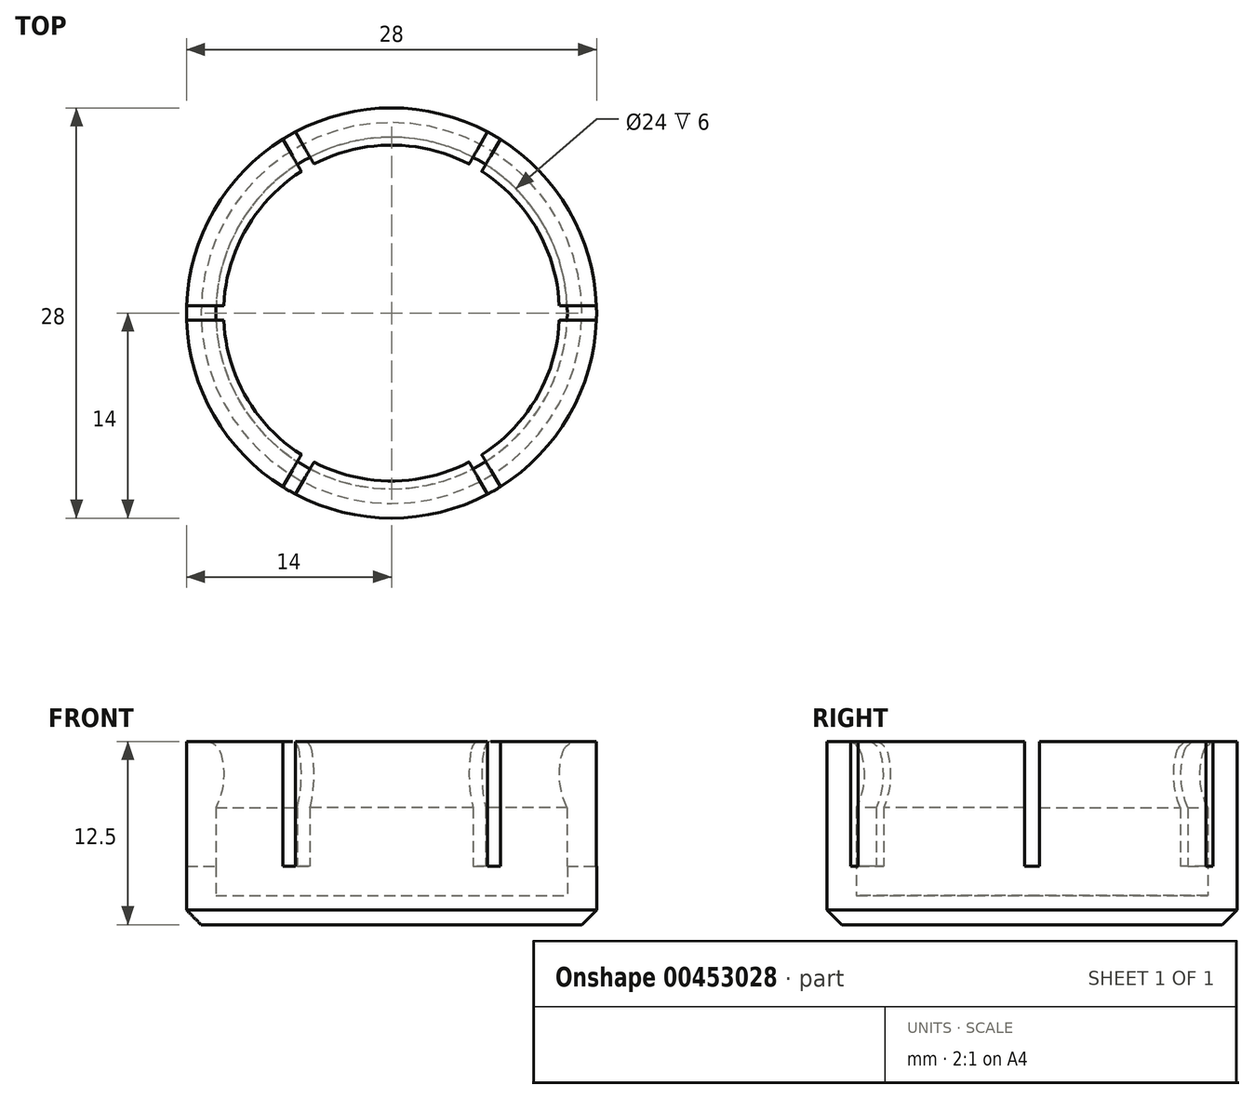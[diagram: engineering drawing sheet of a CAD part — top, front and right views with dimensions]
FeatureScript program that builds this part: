
annotation { "Feature Type Name" : "Feature", "Feature Type Description" : "" }
export const myFeature = defineFeature(function(context is Context, id is Id, definition is map)
    precondition{}
    {
        {
            assignVariable(context, id + "F0", {"name" : "Fase", "anyValue" : 1});
        }
        {
            var Q0;
            Q0=qCreatedBy(makeId("Front.planeOp"),FACE);
            var sketch = newSketch(context, id + "F1", { "sketchPlane" : qUnion([Q0])});
            skLineSegment(sketch, "E0", {"start": v(0, 0) * mm, "end": v(14, 0) * mm});
            skLineSegment(sketch, "E1", {"start": v(14, 0) * mm, "end": v(14, 12.5) * mm});
            skLineSegment(sketch, "E2", {"start": v(14, 12.5) * mm, "end": v(12, 12.5) * mm});
            skLineSegment(sketch, "E3", {"start": v(12, 12.5) * mm, "end": v(12, 2) * mm});
            skLineSegment(sketch, "E4", {"start": v(12, 2) * mm, "end": v(0, 2) * mm});
            skLineSegment(sketch, "E5", {"start": v(12, 2) * mm, "end": v(12, 8) * mm, "construction": true});
            skArc(sketch, "E6", {"start": v(12, 12.5) * mm, "mid": v(11.47, 10.25) * mm, "end": v(12, 8) * mm});
            skLineSegment(sketch, "E7", {"start": v(0, 0) * mm, "end": v(0, 19.05) * mm, "construction": true});
            skLineSegment(sketch, "E8", {"start": v(0, 2) * mm, "end": v(0, 0) * mm});
            skLineSegment(sketch, "E9", {"start": v(11.47, 12.5) * mm, "end": v(11.47, 8) * mm, "construction": true});
            skLineSegment(sketch, "E10", {"start": v(12, 12.5) * mm, "end": v(11.47, 12.5) * mm, "construction": true});
            skLineSegment(sketch, "E11", {"start": v(12, 8) * mm, "end": v(11.47, 8) * mm, "construction": true});
            skSolve(sketch);
        }
        {
            var Q0;
            Q0=makeQuery(id+"F1.imprint","IMPRINT",FACE,{"disambiguationData":[TD([[makeQuery(id+"F1.imprint","IMPRINT",EDGE,{"derivedFrom":sQuery(id+"F1.wireOp",EDGE,"E0")}),1.0]])]});
            var Q1;
            {var subQ0=sQuery(id+"F1.wireOp",EDGE,"E6");Q1=makeQuery(id+"F1.imprint","IMPRINT",FACE,{"disambiguationData":[TD([[makeQuery(id+"F1.imprint","IMPRINT",EDGE,{"derivedFrom":subQ0}),1.0]])]});}
            var Q2;
            Q2=sQuery(id+"F1.wireOp",EDGE,"E7");
            revolve(context, id + "F2", {"entities" : qUnion([Q0, Q1]), "axis" : qUnion([Q2]), "revolveType" : RevolveType.FULL});
        }
        {
            var Q0;
            Q0=makeQuery(id+"F2.opRevolve","SWEPT_EDGE",EDGE,{"disambiguationData":[OSD([sQuery(id+"F1.wireOp",EDGE,"E2"),sQuery(id+"F1.wireOp",EDGE,"E3"),sQuery(id+"F1.wireOp",EDGE,"E6")])]});
            fillet(context, id + "F3", {"entities" : qUnion([Q0]), "radius" : 1 * mm, "tangentPropagation" : true, "allowEdgeOverflow" : false});
        }
        {
            var Q0;
            Q0=makeQuery(id+"F2.opRevolve","SWEPT_EDGE",EDGE,{"disambiguationData":[OSD([sQuery(id+"F1.wireOp",EDGE,"E0"),sQuery(id+"F1.wireOp",EDGE,"E1")])]});
            chamfer(context, id + "F4", {"entities" : qUnion([Q0]), "width" : (getVariable(context, 'Fase')) * mm, "tangentPropagation" : true});
        }
        {
            var Q0;
            Q0=qCreatedBy(makeId("Front.planeOp"),FACE);
            var sketch = newSketch(context, id + "F5", { "sketchPlane" : qUnion([Q0])});
            skLineSegment(sketch, "E12.bottom", {"start": v(-25, 18) * mm, "end": v(25, 18) * mm});
            skLineSegment(sketch, "E12.top", {"start": v(-25, 4) * mm, "end": v(25, 4) * mm});
            skLineSegment(sketch, "E12.left", {"start": v(-25, 18) * mm, "end": v(-25, 4) * mm});
            skLineSegment(sketch, "E12.right", {"start": v(25, 18) * mm, "end": v(25, 4) * mm});
            skLineSegment(sketch, "E13", {"start": v(0, 0) * mm, "end": v(0, 40.33) * mm, "construction": true});
            skSolve(sketch);
        }
        {
            var Q0;
            Q0 = qSketchRegion(id + "F5", true);
            extrude(context, id + "F6", {"entities" : qUnion([Q0]), "depth" : 0.5 * mm, "hasSecondDirection" : true, "secondDirectionOppositeDirection" : true, "secondDirectionDepth" : 0.5 * mm});
        }
        {
            var Q0;
            Q0=makeQuery(id+"F6.opExtrude","SWEPT_BODY",BODY,{"disambiguationData":[OSD([sQuery(id+"F5.wireOp",EDGE,"E12.bottom"),sQuery(id+"F5.wireOp",EDGE,"E12.top"),sQuery(id+"F5.wireOp",EDGE,"E12.left"),sQuery(id+"F5.wireOp",EDGE,"E12.right")])]});
            var Q1;
            Q1=sQuery(id+"F5.wireOp",EDGE,"E13");
            circularPattern(context, id + "F7", {"entities" : qUnion([Q0]), "axis" : qUnion([Q1]), "angle" : 360 * degree, "instanceCount" : 3, "equalSpace" : true});
        }
        {
            var Q0;
            Q0=makeQuery(id+"F7.opPattern","COPY",BODY,{"derivedFrom":makeQuery(id+"F6.opExtrude","SWEPT_BODY",BODY,{"disambiguationData":[OSD([sQuery(id+"F5.wireOp",EDGE,"E12.bottom"),sQuery(id+"F5.wireOp",EDGE,"E12.top"),sQuery(id+"F5.wireOp",EDGE,"E12.left"),sQuery(id+"F5.wireOp",EDGE,"E12.right")])]}),"instanceName":"1"});
            var Q1;
            Q1=makeQuery(id+"F6.opExtrude","SWEPT_BODY",BODY,{"disambiguationData":[OSD([sQuery(id+"F5.wireOp",EDGE,"E12.bottom"),sQuery(id+"F5.wireOp",EDGE,"E12.top"),sQuery(id+"F5.wireOp",EDGE,"E12.left"),sQuery(id+"F5.wireOp",EDGE,"E12.right")])]});
            var Q2;
            Q2=makeQuery(id+"F7.opPattern","COPY",BODY,{"derivedFrom":makeQuery(id+"F6.opExtrude","SWEPT_BODY",BODY,{"disambiguationData":[OSD([sQuery(id+"F5.wireOp",EDGE,"E12.bottom"),sQuery(id+"F5.wireOp",EDGE,"E12.top"),sQuery(id+"F5.wireOp",EDGE,"E12.left"),sQuery(id+"F5.wireOp",EDGE,"E12.right")])]}),"instanceName":"2"});
            var Q3;
            Q3=makeQuery(id+"F2.opRevolve","SWEPT_BODY",BODY,{"disambiguationData":[OSD([sQuery(id+"F1.wireOp",EDGE,"E0"),sQuery(id+"F1.wireOp",EDGE,"E1"),sQuery(id+"F1.wireOp",EDGE,"E2"),sQuery(id+"F1.wireOp",EDGE,"E3"),sQuery(id+"F1.wireOp",EDGE,"E4"),sQuery(id+"F1.wireOp",EDGE,"E6"),sQuery(id+"F1.wireOp",EDGE,"E8")])]});
            booleanBodies(context, id + "F8", {"operationType" : BooleanOperationType.SUBTRACTION, "tools" : qUnion([Q0, Q1, Q2]), "targets" : qUnion([Q3])});
        }
    });
